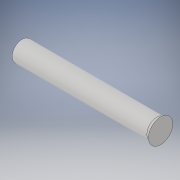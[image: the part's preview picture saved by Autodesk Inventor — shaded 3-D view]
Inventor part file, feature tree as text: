
AUTODESK INVENTOR PART (.ipt)
format: ipt  version: 2018.3 (Build 223284000, 284)  size: 101,888 bytes
history: native  units: in
note: dims shown in document units (in); Inventor stores cm internally (conversion verified against a paired STEP export)
features: revolve x1, sketch x1
ambient origin geometry x8: Origin, YZ Plane, XZ Plane, XY Plane, X Axis, Y Axis, Z Axis, Center Point
bodies: Solid1 (feature_tree)
feature tree (2):
  revolve  "Revolution1"  [1 undecoded]
  sketch  "Sketch1"  dims[d0=0.78in d1=0.067in d2=0.055in d3=210.0deg d4=0.22in d5=90.0deg]
note: 1 required parameter value undecoded (feature->parameter linkage not recoverable at this tier; creation-order binding heuristic only, values carry confidence <= 0.55)
